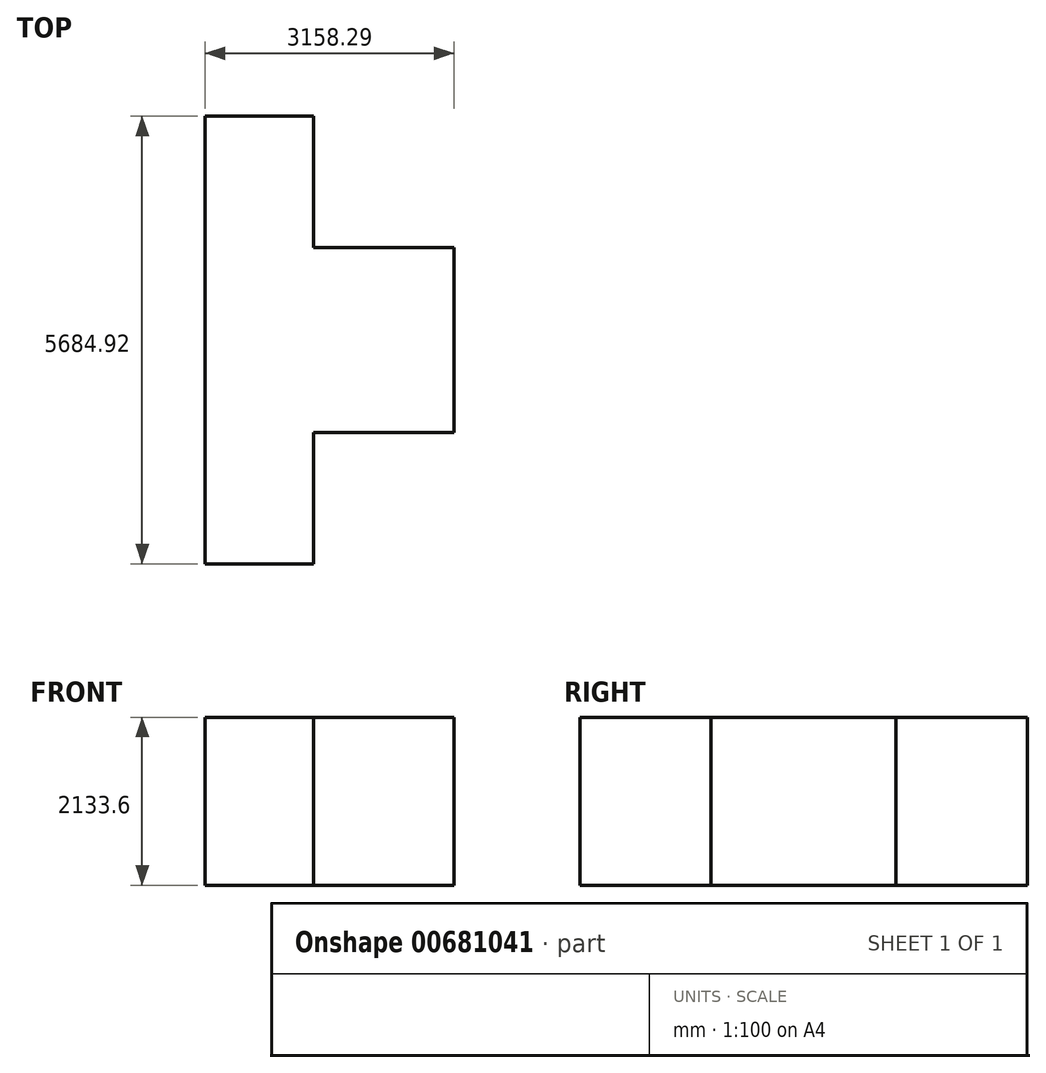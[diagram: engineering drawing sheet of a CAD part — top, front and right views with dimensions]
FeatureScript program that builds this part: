
annotation { "Feature Type Name" : "Feature", "Feature Type Description" : "" }
export const myFeature = defineFeature(function(context is Context, id is Id, definition is map)
    precondition{}
    {
        {
            var Q0;
            Q0=qCreatedBy(makeId("Top.planeOp"),FACE);
            var sketch = newSketch(context, id + "F0", { "sketchPlane" : qUnion([Q0])});
            skLineSegment(sketch, "E0.MirrorCS", {"start": v(0, 13.99) * mm, "end": v(0, 33.84) * mm});
            skLineSegment(sketch, "E1.MirrorCS", {"start": v(-16.4, 0) * mm, "end": v(-16.4, 33.84) * mm});
            skLineSegment(sketch, "E2.MirrorCS", {"start": v(21.2, 13.99) * mm, "end": v(0, 13.99) * mm});
            skLineSegment(sketch, "E3.MirrorCS", {"start": v(21.2, -13.99) * mm, "end": v(0, -13.99) * mm});
            skLineSegment(sketch, "E4.MirrorCS", {"start": v(-16.4, 0) * mm, "end": v(-16.4, -33.84) * mm});
            skLineSegment(sketch, "E5.MirrorCS", {"start": v(0, -13.99) * mm, "end": v(0, -33.84) * mm});
            skLineSegment(sketch, "E6", {"start": v(21.2, 13.99) * mm, "end": v(21.2, -13.99) * mm});
            skLineSegment(sketch, "E7", {"start": v(0, -33.84) * mm, "end": v(-16.4, -33.84) * mm});
            skLineSegment(sketch, "E8", {"start": v(-16.4, 33.84) * mm, "end": v(0, 33.84) * mm});
            skSolve(sketch);
        }
        {
            var Q0;
            Q0=makeQuery(id+"F0.imprint","IMPRINT",FACE,{"disambiguationData":[TD([[makeQuery(id+"F0.imprint","IMPRINT",EDGE,{"derivedFrom":sQuery(id+"F0.wireOp",EDGE,"E0.MirrorCS")}),1.0]])]});
            extrude(context, id + "F1", {"entities" : qUnion([Q0]), "depth" : 25.4 * mm, "offsetDistance" : 25.4 * mm});
        }
        {
            var Q0;
            Q0=makeQuery(id+"F1.opExtrude","SWEPT_BODY",BODY,{"disambiguationData":[OSD([sQuery(id+"F0.wireOp",EDGE,"E0.MirrorCS"),sQuery(id+"F0.wireOp",EDGE,"E1.MirrorCS"),sQuery(id+"F0.wireOp",EDGE,"E2.MirrorCS"),sQuery(id+"F0.wireOp",EDGE,"E3.MirrorCS"),sQuery(id+"F0.wireOp",EDGE,"E4.MirrorCS"),sQuery(id+"F0.wireOp",EDGE,"E5.MirrorCS"),sQuery(id+"F0.wireOp",EDGE,"E6"),sQuery(id+"F0.wireOp",EDGE,"E7"),sQuery(id+"F0.wireOp",EDGE,"E8")])]});
            var Q1;
            Q1=qCreatedBy(makeId("Origin.pointOp"),VERTEX);
            transform(context, id + "F2", {"entities" : qUnion([Q0]), "transformType" : TransformType.SCALE_UNIFORMLY, "scale" : 84, "scalePoint" : qUnion([Q1]), "makeCopy" : false});
        }
    });
